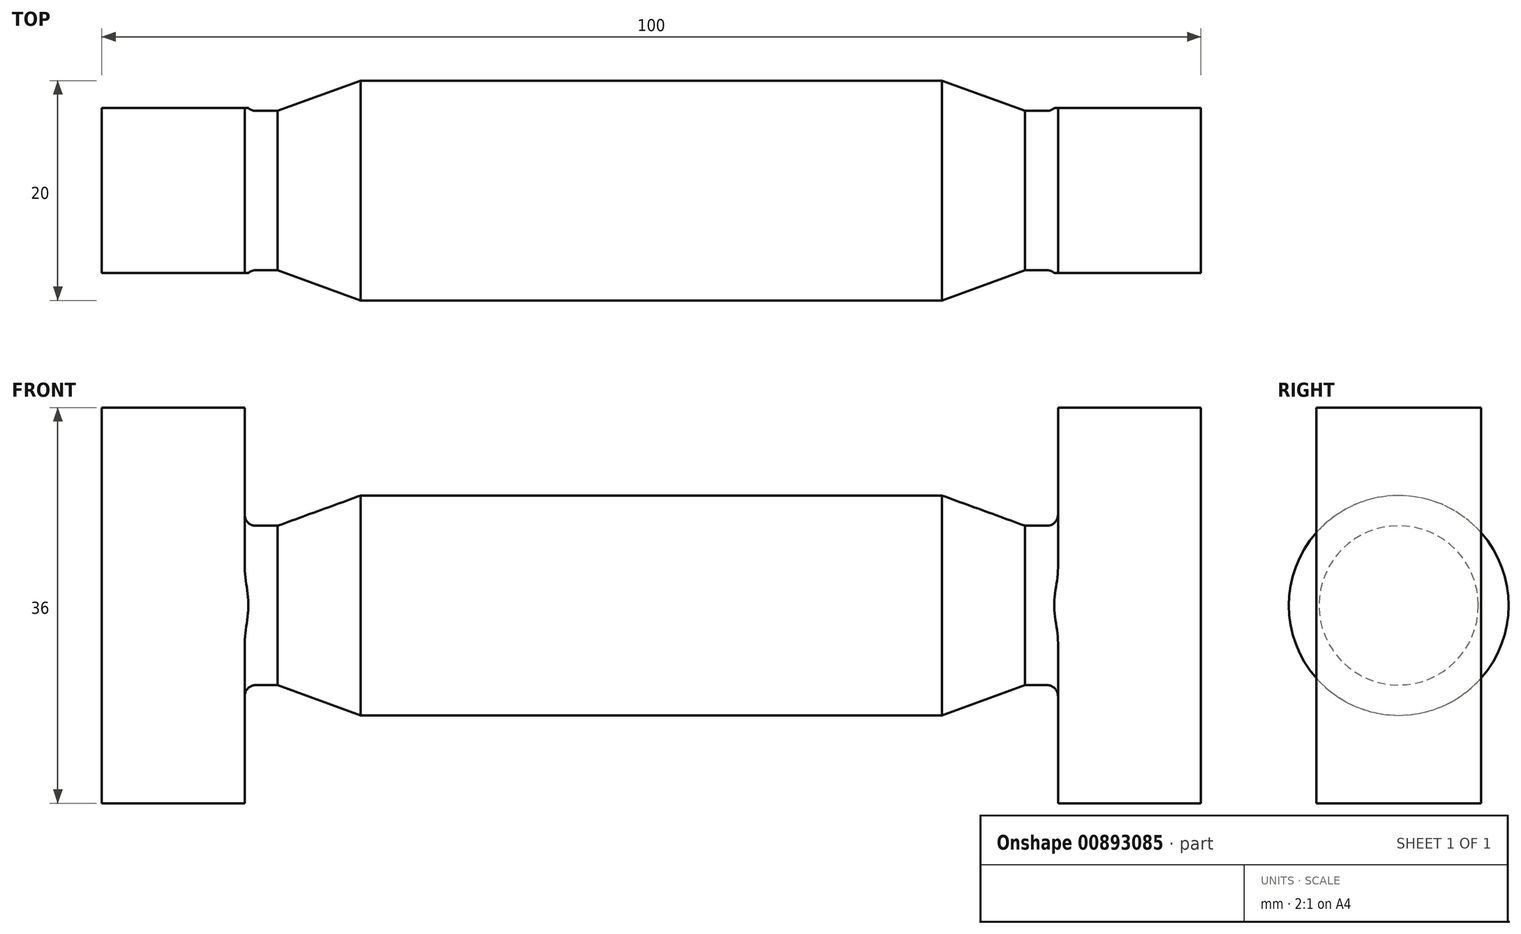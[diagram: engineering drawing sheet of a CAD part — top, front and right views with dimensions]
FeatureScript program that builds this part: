
annotation { "Feature Type Name" : "Feature", "Feature Type Description" : "" }
export const myFeature = defineFeature(function(context is Context, id is Id, definition is map)
    precondition{}
    {
        {
            var Q0;
            Q0=qCreatedBy(makeId("Top.planeOp"),FACE);
            var sketch = newSketch(context, id + "F0", { "sketchPlane" : qUnion([Q0])});
            skLineSegment(sketch, "E0", {"start": v(0, 0) * mm, "end": v(100, 0) * mm});
            skLineSegment(sketch, "E1", {"start": v(100, 0) * mm, "end": v(100, 25) * mm});
            skLineSegment(sketch, "E2", {"start": v(100, 25) * mm, "end": v(87, 25) * mm});
            skLineSegment(sketch, "E3", {"start": v(87, 25) * mm, "end": v(87, 8.25) * mm});
            skLineSegment(sketch, "E4", {"start": v(86, 7.25) * mm, "end": v(84, 7.25) * mm});
            skLineSegment(sketch, "E5", {"start": v(84, 7.25) * mm, "end": v(76.44, 10) * mm});
            skLineSegment(sketch, "E6", {"start": v(76.44, 10) * mm, "end": v(23.56, 10) * mm});
            skLineSegment(sketch, "E7", {"start": v(23.56, 10) * mm, "end": v(16, 7.25) * mm});
            skLineSegment(sketch, "E8", {"start": v(16, 7.25) * mm, "end": v(14, 7.25) * mm});
            skLineSegment(sketch, "E9", {"start": v(13, 8.25) * mm, "end": v(13, 25) * mm});
            skLineSegment(sketch, "E10", {"start": v(13, 25) * mm, "end": v(0, 25) * mm});
            skLineSegment(sketch, "E11", {"start": v(0, 25) * mm, "end": v(0, 0) * mm});
            skLineSegment(sketch, "E12", {"start": v(0, 0) * mm, "end": v(100, 0) * mm, "construction": true});
            skPoint(sketch, "E13.visualSharp", {"position": v(0, 25) * mm});
            skPoint(sketch, "E14.visualSharp", {"position": v(13, 7.25) * mm});
            skArc(sketch, "E14.filletArc", {"start": v(13, 8.25) * mm, "mid": v(13.3, 7.54) * mm, "end": v(14, 7.25) * mm});
            skPoint(sketch, "E15.visualSharp", {"position": v(87, 7.25) * mm});
            skArc(sketch, "E15.filletArc", {"start": v(86, 7.25) * mm, "mid": v(86.7, 7.54) * mm, "end": v(87, 8.25) * mm});
            skSolve(sketch);
        }
        {
            var Q0;
            Q0 = qSketchRegion(id + "F0", true);
            var Q1;
            Q1=sQuery(id+"F0.wireOp",EDGE,"E0");
            revolve(context, id + "F1", {"surfaceOperationType" : NewSurfaceOperationType.NEW, "entities" : qUnion([Q0]), "axis" : qUnion([Q1]), "revolveType" : RevolveType.FULL});
        }
        {
            var Q0;
            Q0=qCreatedBy(makeId("Right.planeOp"),FACE);
            var sketch = newSketch(context, id + "F2", { "sketchPlane" : qUnion([Q0])});
            skLineSegment(sketch, "E16.bottom", {"start": v(7.5, 18) * mm, "end": v(-7.5, 18) * mm});
            skLineSegment(sketch, "E16.top", {"start": v(7.5, -18) * mm, "end": v(-7.5, -18) * mm});
            skLineSegment(sketch, "E16.left", {"start": v(7.5, 18) * mm, "end": v(7.5, -18) * mm});
            skLineSegment(sketch, "E16.right", {"start": v(-7.5, 18) * mm, "end": v(-7.5, -18) * mm});
            skLineSegment(sketch, "E17", {"start": v(7.5, 18) * mm, "end": v(-7.5, -18) * mm, "construction": true});
            skLineSegment(sketch, "E18", {"start": v(-7.5, 18) * mm, "end": v(7.5, -18) * mm, "construction": true});
            skCircle(sketch, "E19", {"center": v(0, 0) * mm, "radius": 37.78 * mm});
            skSolve(sketch);
        }
        {
            var Q0;
            Q0 = qSketchRegion(id + "F2", true);
            var Q1;
            Q1=makeQuery(id+"F1.opRevolve","SWEPT_FACE",FACE,{"disambiguationData":[OSD([sQuery(id+"F0.wireOp",EDGE,"E7")])]});
            extrude(context, id + "F3", {"entities" : qUnion([Q0]), "operationType" : NewBodyOperationType.REMOVE, "endBound" : BoundingType.UP_TO_SURFACE, "depth" : 25 * mm, "endBoundEntityFace" : qUnion([Q1]), "offsetDistance" : 25 * mm});
        }
        {
            var Q0;
            Q0=makeQuery(id+"F1.opRevolve","SWEPT_FACE",FACE,{"disambiguationData":[OSD([sQuery(id+"F0.wireOp",EDGE,"E1")])]});
            var sketch = newSketch(context, id + "F4", { "sketchPlane" : qUnion([Q0])});
            skLineSegment(sketch, "E20.bottom", {"start": v(-7.5, 18) * mm, "end": v(7.5, 18) * mm});
            skLineSegment(sketch, "E20.top", {"start": v(-7.5, -18) * mm, "end": v(7.5, -18) * mm});
            skLineSegment(sketch, "E20.left", {"start": v(-7.5, 18) * mm, "end": v(-7.5, -18) * mm});
            skLineSegment(sketch, "E20.right", {"start": v(7.5, 18) * mm, "end": v(7.5, -18) * mm});
            skCircle(sketch, "E21", {"center": v(0, 0) * mm, "radius": 41.88 * mm});
            skSolve(sketch);
        }
        {
            var Q0;
            Q0 = qSketchRegion(id + "F4", true);
            var Q1;
            Q1=makeQuery(id+"F1.opRevolve","SWEPT_FACE",FACE,{"disambiguationData":[OSD([sQuery(id+"F0.wireOp",EDGE,"E5")])]});
            extrude(context, id + "F5", {"entities" : qUnion([Q0]), "operationType" : NewBodyOperationType.REMOVE, "endBound" : BoundingType.UP_TO_SURFACE, "oppositeDirection" : true, "depth" : 25 * mm, "endBoundEntityFace" : qUnion([Q1]), "offsetDistance" : 25 * mm});
        }
    });
